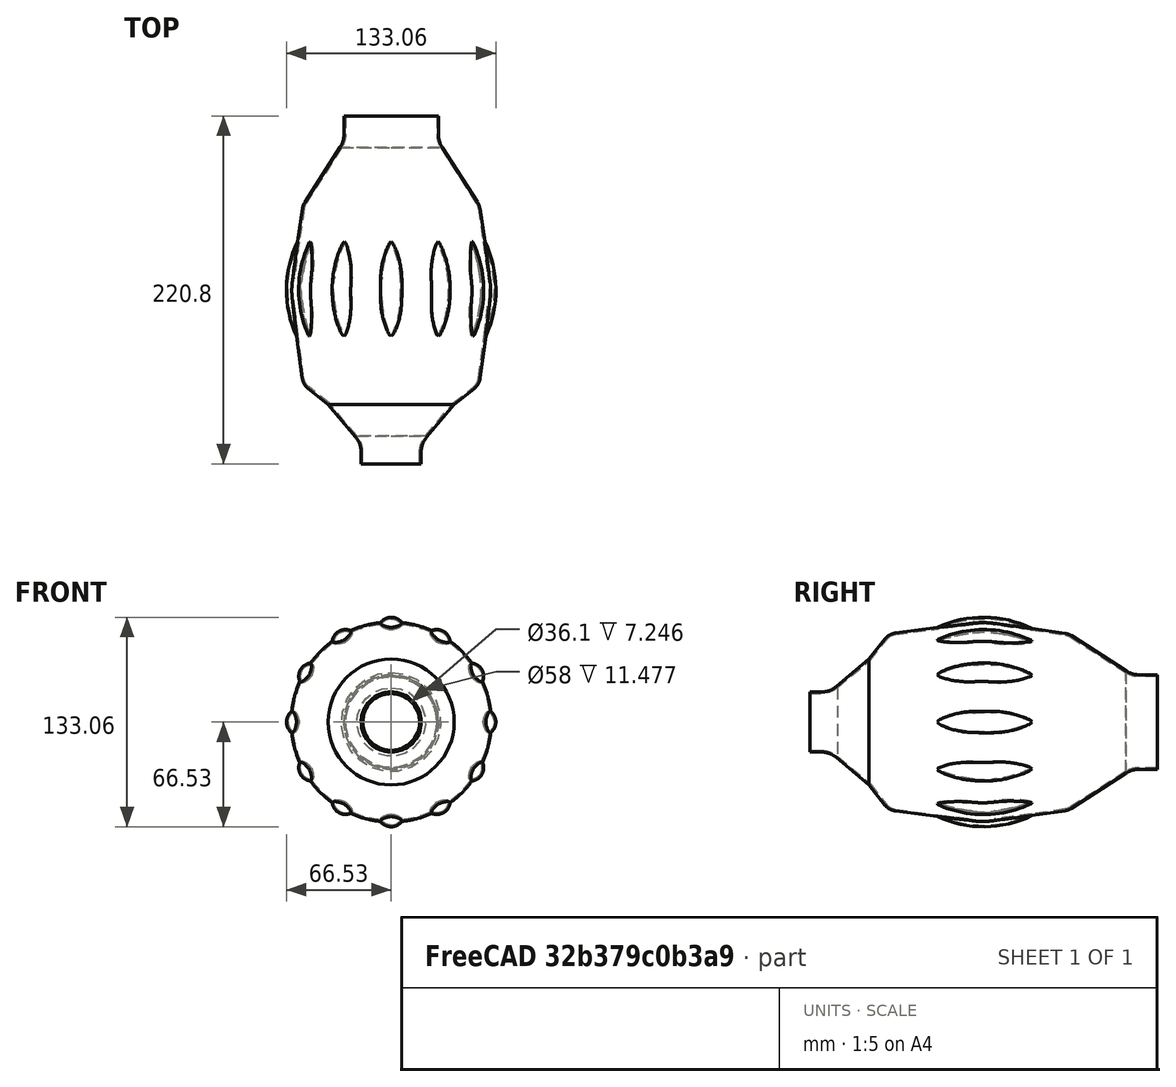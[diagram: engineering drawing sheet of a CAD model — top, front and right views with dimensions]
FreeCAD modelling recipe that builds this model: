
FCSTD DOCUMENT  (FreeCAD 0.18R4 (GitTag))
Label: PressureBag OpenLung
License: All rights reserved
LicenseURL: http://en.wikipedia.org/wiki/All_rights_reserved
objects: PartDesign::Fillet×3, Sketcher::SketchObject×2, PartDesign::Revolution×2, App::Part×2, Mesh::Feature×1, PartDesign::Line×1, PartDesign::PolarPattern×1, PartDesign::Thickness×1, PartDesign::Body×1
note: 13 computed .brp shape members not serialized (recipe doc carries the construction recipe); baked Part::Feature solids carry a one-line shape summary decoded from their .brp

FEATURE [Sketcher::SketchObject] Sketch
  MapMode = 5
  Placement = pos=(0,0,0) rot=(0.57735,0.57735,0.57735;2.0944rad)
  Support = -> [YZ_Plane009]
  sketch-geometry (10):
    g0: LineSegment StartX=-110.4 StartY=19.05 StartZ=0 EndX=-97.7 EndY=19.05 EndZ=0
    g1: LineSegment StartX=-110.4 StartY=19.05 StartZ=0 EndX=-110.4 EndY=0 EndZ=0
    g2: LineSegment StartX=-110.4 StartY=0 StartZ=0 EndX=110.4 EndY=0 EndZ=0
    g3: LineSegment StartX=110.4 StartY=0 StartZ=0 EndX=110.4 EndY=30 EndZ=0
    g4: LineSegment StartX=110.4 StartY=30 StartZ=0 EndX=94.525 EndY=30 EndZ=0
    g5: LineSegment StartX=-97.7 StartY=19.05 StartZ=0 EndX=-72.7 EndY=40 EndZ=0
    g6: LineSegment StartX=-72.7 StartY=40 StartZ=0 EndX=-60 EndY=56 EndZ=0
    g7: LineSegment StartX=-60 StartY=56 StartZ=0 EndX=0 EndY=64 EndZ=0
    g8: LineSegment StartX=0 StartY=64 StartZ=0 EndX=54 EndY=56 EndZ=0
    g9: LineSegment StartX=54 StartY=56 StartZ=0 EndX=94.525 EndY=30 EndZ=0
  constraints (29):
    c: Horizontal(g0)
    c: Coincident(g0,g1)
    c: PointOnObject(g1,g-1)
    c: Coincident(g1,g2)
    c: Coincident(g2,g3)
    c: Coincident(g3,g4)
    c: Horizontal(g4)
    c: Vertical(g3)
    c: Symmetric(g2,g1,g-1)
    c: Vertical(g1)
    c: DistanceY(g1,g1) = 19.05
    c: DistanceX(g0,g0) = 12.7
    c: DistanceX(g4,g4) = 15.875
    c: Coincident(g0,g5)
    c: Coincident(g5,g6)
    c: Coincident(g6,g7)
    c: PointOnObject(g7,g-2)
    c: Coincident(g7,g8)
    c: Coincident(g8,g9)
    c: Coincident(g9,g4)
    c: DistanceX(g0,g5) = 25
    c: DistanceX(g5,g6) = 12.7
    c: DistanceX(g6,g7) = 60
    c: DistanceX(g7,g8) = 54
    c: DistanceY(g-1,g5) = 40
    c: DistanceY(g-1,g6) = 56
    c: DistanceY(g-1,g7) = 64
    c: DistanceY(g-1,g8) = 56
    c: DistanceY(g-1,g4) = 30
FEATURE [PartDesign::Revolution] Revolution
  Angle = 360
  Axis = (3e-16,1,-2e-16)
  Base = (0,0,0)
  Placement = pos=(0,0,0) rot=(0.57735,0.57735,0.57735;2.0944rad)
  Profile = -> Sketch
  ReferenceAxis = -> Sketch [H_Axis]
  Refine = true
FEATURE [Mesh::Feature] openlungbag
  Placement = pos=(0,-112,-66) rot=(0,0,1;0rad)
FEATURE [Sketcher::SketchObject] Sketch001
  MapMode = 5
  Support = -> [XY_Plane009]
  sketch-geometry (4):
    g0: ArcOfCircle CenterX=-3.47086 CenterY=1.07e-14 CenterZ=0 NormalX=0 NormalY=0 NormalZ=1 AngleXU=0 Radius=70 StartAngle=5.78438 EndAngle=6.78199
    g1: LineSegment [constr] StartX=58 StartY=33.4863 StartZ=0 EndX=0 EndY=0 EndZ=0
    g2: LineSegment [constr] StartX=0 StartY=0 StartZ=0 EndX=58 EndY=-33.4863 EndZ=0
    g3: LineSegment StartX=58 StartY=33.4863 StartZ=0 EndX=58 EndY=-33.4863 EndZ=0
  constraints (10):
    c: Radius(g0) = 70
    c: Symmetric(g0,g0,g-1)
    c: Coincident(g0,g1)
    c: Coincident(g1,g2)
    c: Coincident(g2,g0)
    c: DistanceX(g1,g0) = 58
    c: Coincident(g-1,g1)
    c: Angle(g2,g1) = 1.0472
    c: Coincident(g3,g0)
    c: Coincident(g0,g3)
FEATURE [PartDesign::Line] DatumLine
  AttacherType = Attacher::AttachEngineLine
  MapMode = 29
  Placement = pos=(58,-2.13e-14,0) rot=(1,0,0;1.5708rad)
  Support = -> [Sketch001]
FEATURE [PartDesign::Revolution] Revolution001
  Angle = 360
  Axis = (-4e-16,-1,2e-16)
  Base = (58,-2.13e-14,0)
  BaseFeature = -> Revolution
  Placement = pos=(0,0,0) rot=(0.57735,0.57735,0.57735;2.0944rad)
  Profile = -> Sketch001
  ReferenceAxis = -> DatumLine
  Refine = true
FEATURE [PartDesign::PolarPattern] PolarPattern
  Angle = 360
  Axis = -> Y_Axis009
  BaseFeature = -> Revolution001
  Occurrences = 12
  Originals = -> [Revolution001]
  Placement = pos=(0,0,0) rot=(0.57735,0.57735,0.57735;2.0944rad)
  Refine = true
FEATURE [PartDesign::Fillet] Fillet
  Base = -> PolarPattern [Edge25,Edge28,Edge22,Edge19,Edge16,Edge13,Edge10,Edge43,Edge40,Edge37,Edge34,Edge31]
  BaseFeature = -> PolarPattern
  Placement = pos=(0,0,0) rot=(0.57735,0.57735,0.57735;2.0944rad)
  Radius = 50
FEATURE [PartDesign::Fillet] Fillet001
  Base = -> Fillet [Edge5,Edge114]
  BaseFeature = -> Fillet
  Placement = pos=(0,0,0) rot=(0.57735,0.57735,0.57735;2.0944rad)
  Radius = 10
FEATURE [PartDesign::Fillet] Fillet002
  Base = -> Fillet001 [Edge117,Edge124]
  BaseFeature = -> Fillet001
  Placement = pos=(0,0,0) rot=(0.57735,0.57735,0.57735;2.0944rad)
  Radius = 15
FEATURE [PartDesign::Thickness] Thickness
  Base = -> Fillet002 [Face49,Face6]
  BaseFeature = -> Fillet002
  Join = 0
  Mode = 0
  Reversed = true
  Value = 1
FEATURE [PartDesign::Body] Body
  Group = -> [Sketch,Revolution,Sketch001,DatumLine,Revolution001,PolarPattern,Fillet,Fillet001,Fillet002,Thickness]
  Origin = -> Origin009
  Tip = -> Thickness
FEATURE [App::Part] Part002  label="Balloon"
  Group = -> [Body]
  Origin = -> Origin004
FEATURE [App::Part] Part  label="Respirator"
  Group = -> [Part002]
  Origin = -> Origin
